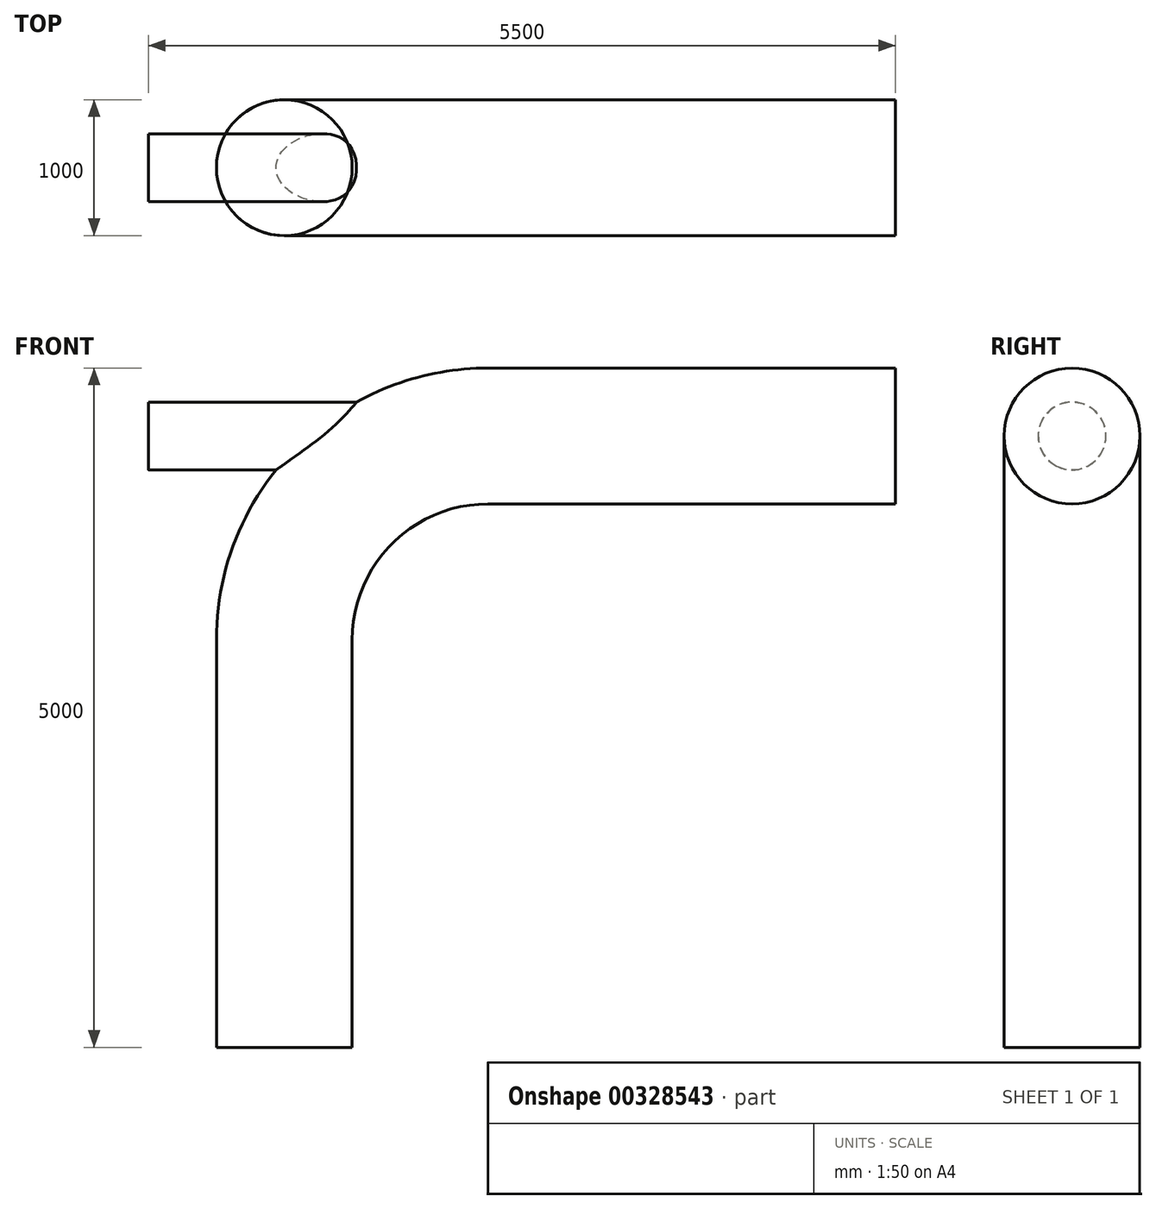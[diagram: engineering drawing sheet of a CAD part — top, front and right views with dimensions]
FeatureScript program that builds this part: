
annotation { "Feature Type Name" : "Feature", "Feature Type Description" : "" }
export const myFeature = defineFeature(function(context is Context, id is Id, definition is map)
    precondition{}
    {
        {
            var Q0;
            Q0=qCreatedBy(makeId("Front.planeOp"),FACE);
            var sketch = newSketch(context, id + "F0", { "sketchPlane" : qUnion([Q0])});
            skLineSegment(sketch, "E0", {"start": v(0, 0) * mm, "end": v(0, 3000) * mm});
            skArc(sketch, "E1", {"start": v(1500, 4500) * mm, "mid": v(439.34, 4060.66) * mm, "end": v(0, 3000) * mm});
            skLineSegment(sketch, "E2", {"start": v(1500, 4500) * mm, "end": v(4500, 4500) * mm});
            skSolve(sketch);
        }
        {
            var Q0;
            Q0=qCreatedBy(makeId("Top.planeOp"),FACE);
            var sketch = newSketch(context, id + "F1", { "sketchPlane" : qUnion([Q0])});
            skCircle(sketch, "E3", {"center": v(0, 0) * mm, "radius": 500 * mm});
            skSolve(sketch);
        }
        {
            var Q0;
            Q0 = qSketchRegion(id + "F1", true);
            var Q1;
            Q1 = qConstructionFilter(qBodyType(qCreatedBy(id + "F0" ,EDGE), BodyType.WIRE), ConstructionObject.NO);
            sweep(context, id + "F2", {"profiles" : qUnion([Q0]), "path" : qUnion([Q1])});
        }
        {
            var Q0;
            Q0=qCreatedBy(makeId("Right.planeOp"),FACE);
            cPlane(context, id + "F3", {"entities" : qUnion([Q0]), "cplaneType" : CPlaneType.OFFSET, "offset" : 1000 * mm, "oppositeDirection" : true, "width" : 150 * mm, "height" : 150 * mm});
        }
        {
            var Q0;
            Q0=qCreatedBy(id+"F3.planeOp",FACE);
            var sketch = newSketch(context, id + "F4", { "sketchPlane" : qUnion([Q0])});
            skCircle(sketch, "E4", {"center": v(0, 4500) * mm, "radius": 250 * mm});
            skSolve(sketch);
        }
        {
            var Q0;
            Q0 = qSketchRegion(id + "F4", true);
            extrude(context, id + "F5", {"entities" : qUnion([Q0]), "operationType" : NewBodyOperationType.ADD, "depth" : 3000 * mm});
        }
    });
